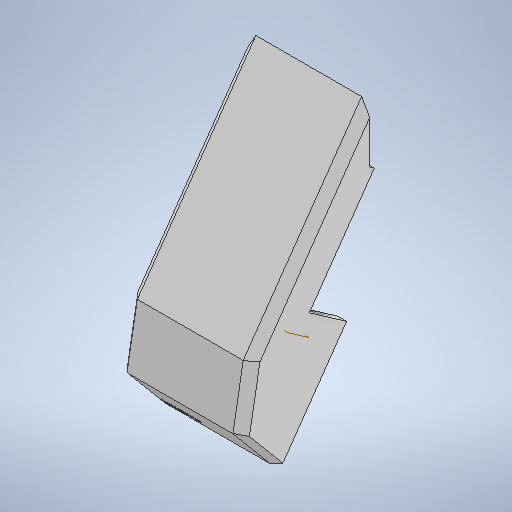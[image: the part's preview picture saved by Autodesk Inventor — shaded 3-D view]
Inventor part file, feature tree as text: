
AUTODESK INVENTOR PART (.ipt)
format: ipt  version: 2025.2 (Build 292293000, 293)  size: 1,433,088 bytes
history: native  units: in
note: dims shown in document units (in); Inventor stores cm internally (conversion verified against a paired STEP export)
features: sketch x46, extrude x41, projected_geometry x15, plane x9, move_body x1, chamfer x1, fillet x1, thicken_offset x1, hole x1
ambient origin geometry x8: Origin, YZ Plane, XZ Plane, XY Plane, X Axis, Y Axis, Z Axis, Center Point
bodies: Solid1 (feature_tree)
feature tree (116):
  extrude  "Extrusion1"  Depth=0.1969in TaperAngle=0.0deg
  move_body  "Move Body1"
  plane  "Work Plane1"
  sketch  "Sketch5"  dims[d5=1.7717in d6=1.7717in d7=1.7717in d8=1.7717in d9=0.8108in d10=90.0deg d11=0.0787in d12=0.3701in d13=0.4252in d14=0.1362in d15=-0.0984in d16=-0.0591in d17=0.0in]
  plane  "Work Plane2"
  extrude  "Extrusion4"  TaperAngle=0.0deg  [1 undecoded]
  extrude  "Extrusion6"  Depth=0.2405in
  extrude  "Extrusion8"  Depth=2.5591in TaperAngle=0.0deg
  chamfer  "Chamfer1"  [1 undecoded]
  extrude  "Extrusion11"  Depth=0.2362in
  plane  "Work Plane3"
  plane  "Work Plane7"
  extrude  "Extrusion22"  Depth=0.1969in TaperAngle=0.0deg
  extrude  "Extrusion25"  Depth=0.5027in
  extrude  "Extrusion26"  Depth=0.5027in
  sketch  "Sketch33"  dims[d96=0.2362in d97=0.0in d100=3.6403in]
  extrude  "Extrusion27"  Depth=0.2362in TaperAngle=0.0deg
  extrude  "Extrusion28"  Depth=3.6403in
  sketch  "Sketch36"  dims[d123=0.9331in d124=0.9712in d125=0.0in]
  extrude  "Extrusion29"  Depth=1.9685in
  extrude  "Extrusion30"  Depth=0.1575in
  extrude  "Extrusion31"  Depth=0.9712in TaperAngle=0.0deg
  sketch  "Sketch39"  dims[d138=0.4331in d139=0.1181in d140=0.0in]
  extrude  "Extrusion32"  Depth=11.3469in TaperAngle=0.0deg
  fillet  "Fillet1"  Radius=11.3469in
  extrude  "Extrusion33"  Depth=0.4331in
  extrude  "Extrusion34"  Depth=0.1181in TaperAngle=0.0deg
  extrude  "Extrusion35"  Depth=0.0787in
  plane  "Work Plane8"
  sketch  "Sketch45"  dims[d160=0.1181in d161=0.0in d162=0.1969in d163=0.0in d164=0.1181in d165=0.0in]
  extrude  "Extrusion37"  Depth=0.2756in
  extrude  "Extrusion38"  Depth=0.1181in TaperAngle=0.0deg
  extrude  "Extrusion40"  Depth=0.5906in
  extrude  "Extrusion41"  Depth=0.1181in TaperAngle=0.0deg
  extrude  "Extrusion43"  Depth=4.7244in TaperAngle=0.0deg
  extrude  "Extrusion44"  Depth=0.7313in TaperAngle=0.0deg
  extrude  "Extrusion46"  TaperAngle=0.0deg  [1 undecoded]
  extrude  "Extrusion48"  Depth=1.1024in
  extrude  "Extrusion50"  Depth=0.0394in TaperAngle=0.0deg
  extrude  "Extrusion51"  Depth=5.8937in TaperAngle=0.0deg
  extrude  "Extrusion53"  Depth=2.3622in TaperAngle=0.0deg
  plane  "Work Plane9"
  plane  "Work Plane12"
  extrude  "Extrusion65"  Depth=0.1969in
  plane  "Work Plane13"
  extrude  "Extrusion67"  TaperAngle=60.0deg  [1 undecoded]
  plane  "Work Plane14"
  extrude  "Extrusion68"  Depth=0.7902in
  extrude  "Extrusion69"  Depth=0.3436in
  extrude  "Extrusion70"  Depth=0.2362in
  sketch  "Sketch84"  dims[d298=0.2362in d299=0.0in d300=0.2362in d301=0.0in]
  extrude  "Extrusion71"  TaperAngle=0.0deg  [1 undecoded]
  extrude  "Extrusion72"  Depth=0.2362in TaperAngle=0.0deg
  extrude  "Extrusion73"  TaperAngle=90.0deg  [1 undecoded]
  extrude  "Extrusion74"  Depth=0.2362in TaperAngle=0.0deg
  extrude  "Extrusion75"  TaperAngle=0.0deg  [1 undecoded]
  extrude  "Extrusion76"  Depth=0.0787in
  thicken_offset  "Thicken1"
  extrude  "Extrusion77"  Depth=0.0787in
  extrude  "Extrusion78"  Depth=0.0787in
  sketch  "Sketch1"  dims[d1=0.5512in d2=0.1969in d3=0.0in]
  sketch  "Sketch6"  dims[d18=0.2749in d24=0.2405in]
  sketch  "Sketch8"  dims[d25=2.7559in d26=0.0in d29=2.5591in d30=0.0in d36=0.0in d37=0.0in]
  sketch  "Sketch12"  dims[d42=0.2362in d43=0.2362in]
  sketch  "Sketch15"  dims[d52=0.2362in d53=0.0787in d54=45.0deg d55=0.1969in d56=0.0in]
  sketch  "Sketch28"  dims[d76=0.5027in d77=0.5027in]
  sketch  "Sketch31"  dims[d78=0.5027in d79=0.5027in]
  sketch  "Sketch32"  dims[d83=0.0in d84=0.0in d94=0.2362in d95=0.0in]
  sketch  "Sketch34"  dims[d101=2.7717in d112=1.9685in]
  sketch  "Sketch35"  dims[d113=0.6299in d114=0.0in d115=0.1575in d117=0.1575in d121=1.9685in d122=0.7874in]
  sketch  "Sketch37"  dims[d126=0.5906in d127=0.0in d128=11.3469in d129=0.0in d130=11.3469in d131=0.0in]
  sketch  "Sketch38"  dims[d136=0.4331in d137=0.4331in]
  sketch  "Sketch40"  dims[d141=0.6299in d142=0.0787in]
  sketch  "Sketch41"  dims[d147=0.2756in d149=0.2756in]
  sketch  "Sketch42"  dims[d150=0.0in d151=0.0in d154=0.1181in d155=0.0in]
  sketch  "Sketch44"  dims[d156=0.1181in d157=0.0in d158=0.5906in]
  projected_geometry  "Projected Loop2"
  projected_geometry  "Projected Loop3"
  projected_geometry  "Projected Loop5"
  sketch  "Sketch47"  dims[d168=0.5906in d169=0.0in d170=4.7244in d171=0.0in]
  sketch  "Sketch49"  dims[d174=0.0in d175=0.0in d176=0.7313in d177=0.0in]
  sketch  "Sketch50"  dims[d186=0.0in d187=0.0in d188=0.0in d189=0.0in]
  sketch  "Sketch52"  dims[d194=0.0in d195=0.0in d196=1.1024in]
  sketch  "Sketch53"  dims[d197=0.5906in d200=0.0394in d201=0.0in]
  sketch  "Sketch56"  dims[d218=0.0in d219=0.0in d220=5.8937in d221=0.0in]
  sketch  "Sketch59"  dims[d233=0.9963in d234=2.3622in d235=0.0in]
  sketch  "Sketch60"  dims[d266=0.1378in d268=0.1969in]
  sketch  "Sketch61"  dims[d269=0.1378in d270=60.0deg]
  sketch  "Sketch63"  dims[d271=4.5565in d272=0.0in d277=0.7902in]
  projected_geometry  "Projected Loop8"
  sketch  "Sketch76"  dims[d278=0.5906in d279=1.378in d280=0.0in d281=0.0in d282=0.3436in]
  sketch  "Sketch78"  dims[d283=1.378in d284=0.9843in d285=0.0in d286=0.0in d287=0.2362in]
  projected_geometry  "Projected Loop14"
  sketch  "Sketch79"  dims[d288=0.0in d289=0.0in d290=0.0in d291=0.0in]
  projected_geometry  "Projected Loop15"
  projected_geometry  "Projected Loop16"
  projected_geometry  "Projected Loop17"
  sketch  "Sketch80"  dims[d292=0.5894in d293=0.2362in d294=0.0in]
  projected_geometry  "Projected Loop18"
  projected_geometry  "Projected Loop20"
  sketch  "Sketch83"  dims[d295=0.2362in d296=0.0in d297=90.0deg]
  projected_geometry  "Projected Loop22"
  sketch  "Sketch85"  dims[d302=0.0787in d303=0.0in d304=0.0in d305=0.0in]
  sketch  "Sketch86"  dims[d306=0.0787in d307=0.0787in]
  sketch  "Sketch87"  dims[d308=0.0787in d309=0.0787in]
  sketch  "Sketch88"  dims[d310=0.0787in d311=0.0787in]
  sketch  "Sketch89"  dims[d312=0.1181in d313=0.0in d314=0.1181in d315=0.0in]
  sketch  "Sketch90"  dims[d38=0.0197in]
  projected_geometry  "Projected Loop23"
  sketch  "Sketch91"  dims[d39=0.0344in]
  projected_geometry  "Projected Loop24"
  sketch  "Sketch92"  dims[d57=0.0197in d58=0.0344in d59=0.0197in d60=0.0344in d81=0.0197in d82=0.0344in d159=0.0344in d178=0.0in d179=0.0in d180=0.0in d181=0.0in d202=0.0197in d203=0.0344in d222=0.0197in d223=0.0344in]
  projected_geometry  "Projected Loop25"
  projected_geometry  "Projected Loop26"
  sketch  "Sketch2"  dims[d4=0.315in]
  hole  "Hole1"  [1 undecoded]
note: 8 required parameter values undecoded (feature->parameter linkage not recoverable at this tier; creation-order binding heuristic only, values carry confidence <= 0.55)
